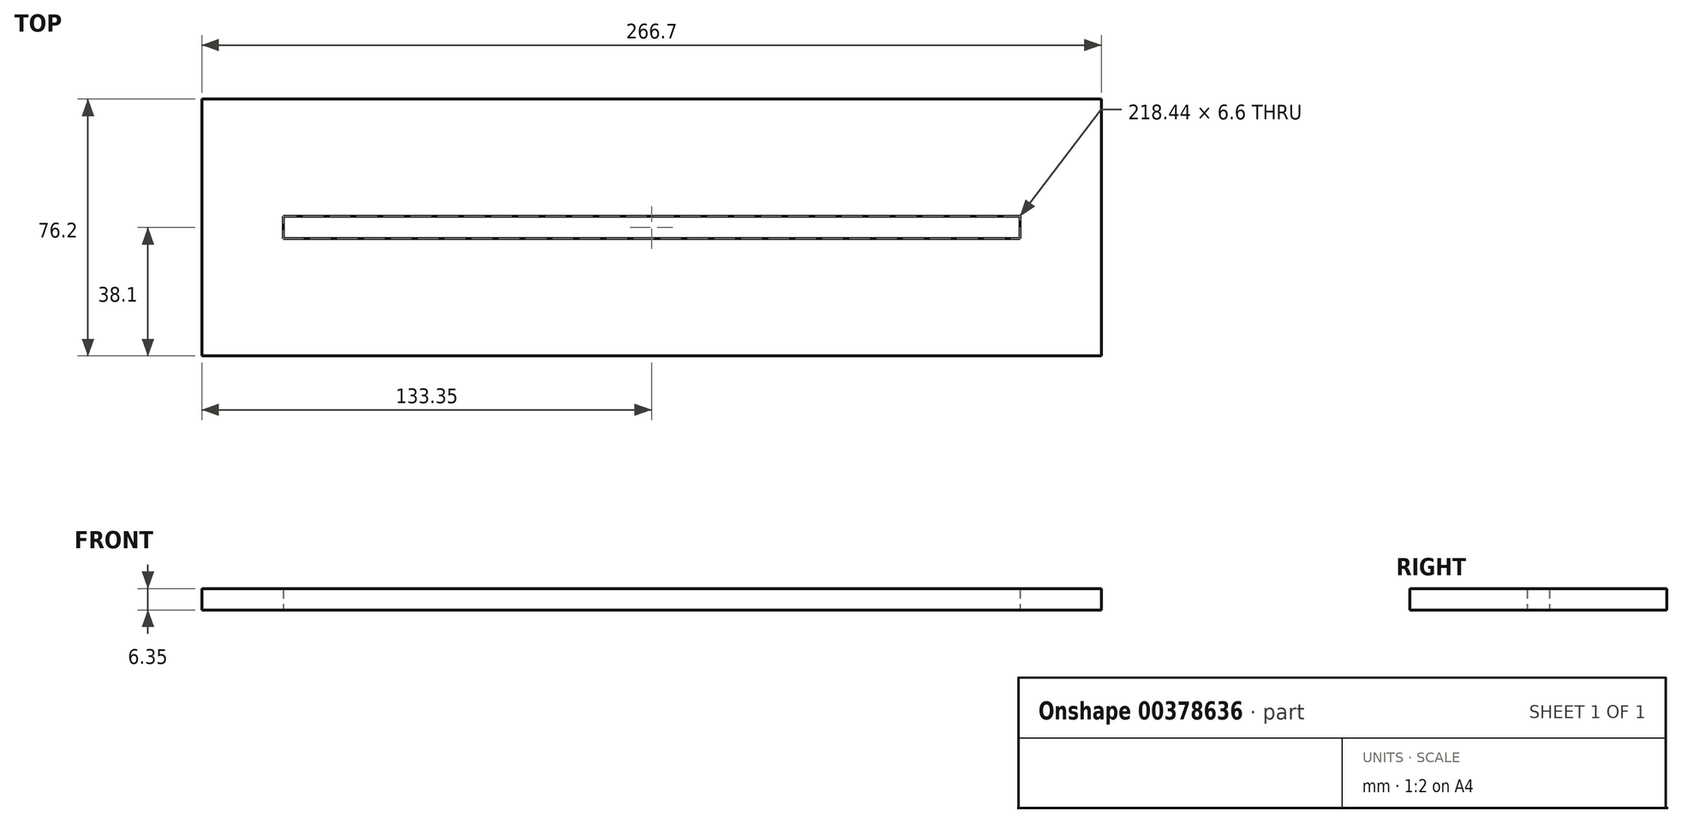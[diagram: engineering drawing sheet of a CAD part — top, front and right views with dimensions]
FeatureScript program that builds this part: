
annotation { "Feature Type Name" : "Feature", "Feature Type Description" : "" }
export const myFeature = defineFeature(function(context is Context, id is Id, definition is map)
    precondition{}
    {
        {
            var Q0;
            Q0=qCreatedBy(makeId("Top.planeOp"),FACE);
            var sketch = newSketch(context, id + "F0", { "sketchPlane" : qUnion([Q0])});
            skLineSegment(sketch, "E0.bottom", {"start": v(-133.35, 38.1) * mm, "end": v(133.35, 38.1) * mm});
            skLineSegment(sketch, "E0.top", {"start": v(-133.35, -38.1) * mm, "end": v(133.35, -38.1) * mm});
            skLineSegment(sketch, "E0.left", {"start": v(-133.35, 38.1) * mm, "end": v(-133.35, -38.1) * mm});
            skLineSegment(sketch, "E0.right", {"start": v(133.35, 38.1) * mm, "end": v(133.35, -38.1) * mm});
            skPoint(sketch, "E0.middle", {"position": v(0, 0) * mm});
            skLineSegment(sketch, "E1.bottom", {"start": v(-109.22, 3.3) * mm, "end": v(109.22, 3.3) * mm});
            skLineSegment(sketch, "E1.top", {"start": v(-109.22, -3.3) * mm, "end": v(109.22, -3.3) * mm});
            skLineSegment(sketch, "E1.left", {"start": v(-109.22, 3.3) * mm, "end": v(-109.22, -3.3) * mm});
            skLineSegment(sketch, "E1.right", {"start": v(109.22, 3.3) * mm, "end": v(109.22, -3.3) * mm});
            skSolve(sketch);
        }
        {
            var Q0;
            Q0=makeQuery(id+"F0.imprint","IMPRINT",FACE,{"disambiguationData":[TD([[makeQuery(id+"F0.imprint","IMPRINT",EDGE,{"derivedFrom":sQuery(id+"F0.wireOp",EDGE,"E0.bottom")}),-1.0]])]});
            extrude(context, id + "F1", {"entities" : qUnion([Q0]), "depth" : 6.35 * mm});
        }
    });
